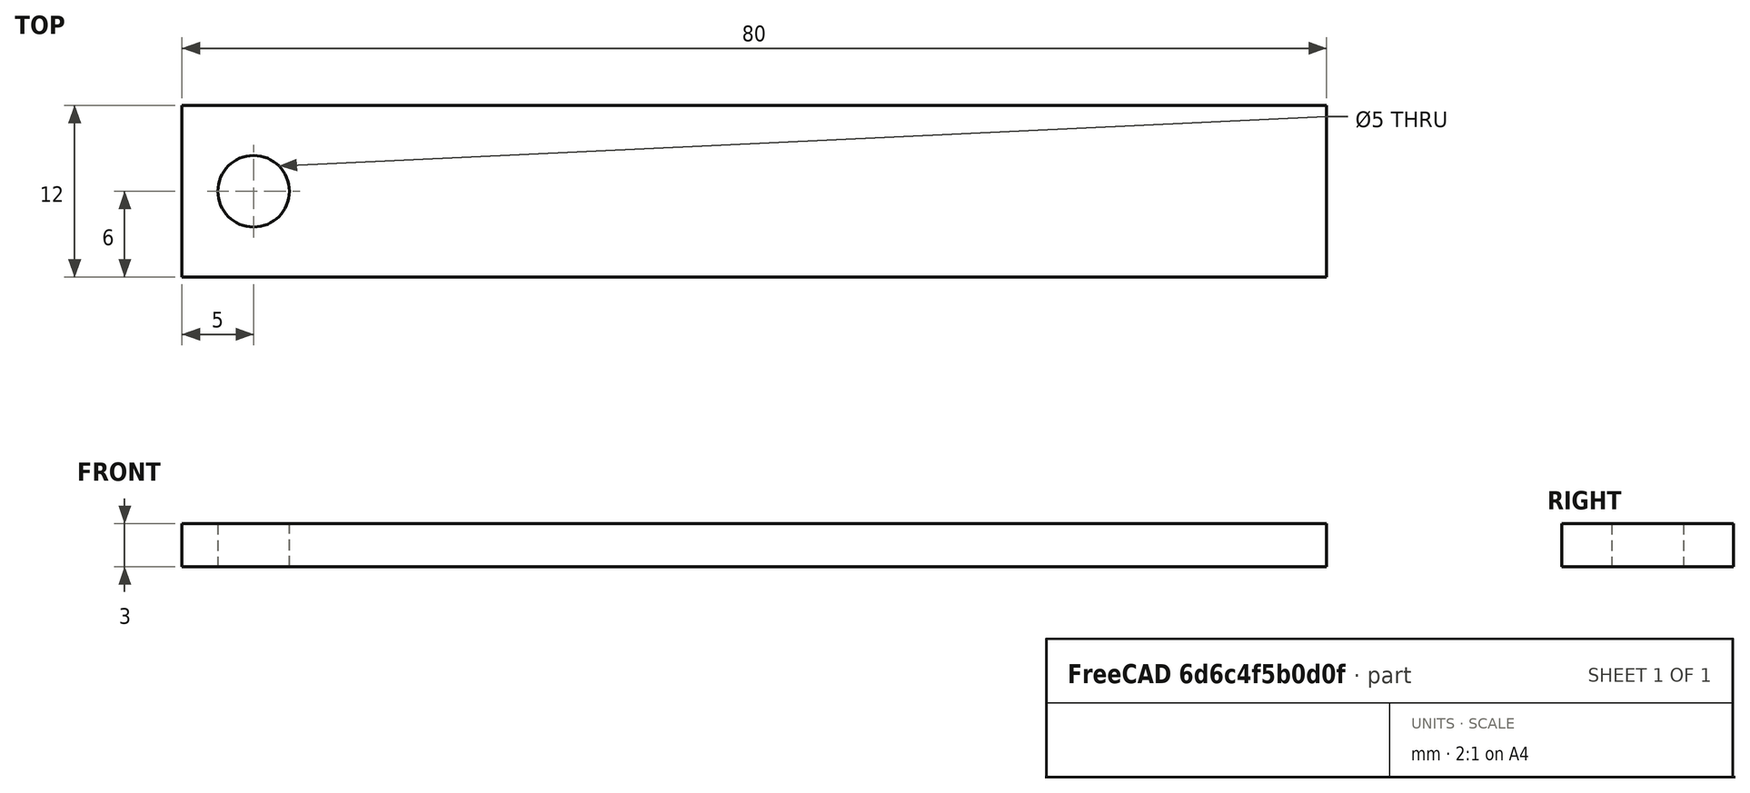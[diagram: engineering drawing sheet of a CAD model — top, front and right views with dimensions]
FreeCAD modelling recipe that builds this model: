
FCSTD DOCUMENT  (FreeCAD 0.20R29177 +426 (Git))
Label: rectangle
License: All rights reserved
LicenseURL: http://en.wikipedia.org/wiki/All_rights_reserved
objects: Sketcher::SketchObject×1, Part::Extrusion×1, PartDesign::Line×1, App::Part×1
note: 3 computed .brp shape members not serialized (recipe doc carries the construction recipe); baked Part::Feature solids carry a one-line shape summary decoded from their .brp

FEATURE [Sketcher::SketchObject] Sketch
  FullyConstrained = true
  sketch-geometry (6):
    g0: LineSegment StartX=40 StartY=-6 StartZ=0 EndX=40 EndY=6 EndZ=0
    g1: LineSegment StartX=40 StartY=6 StartZ=0 EndX=-40 EndY=6 EndZ=0
    g2: LineSegment StartX=-40 StartY=6 StartZ=0 EndX=-40 EndY=-6 EndZ=0
    g3: LineSegment StartX=-40 StartY=-6 StartZ=0 EndX=40 EndY=-6 EndZ=0
    g4: GeomPoint X=0 Y=0 Z=0
    g5: Circle CenterX=-35 CenterY=0 CenterZ=0 NormalX=0 NormalY=0 NormalZ=1 AngleXU=0 Radius=2.5
  constraints (15):
    c: Coincident(g0,g1)
    c: Coincident(g1,g2)
    c: Coincident(g2,g3)
    c: Coincident(g3,g0)
    c: Horizontal(g1)
    c: Horizontal(g3)
    c: Vertical(g0)
    c: Vertical(g2)
    c: Symmetric(g1,g0,g4)
    c: Coincident(g4,g-1)
    c: DistanceX(g1,g1) = 80
    c: DistanceY(g2,g2) = 12
    c: DistanceX(g1,g5) = 5
    c: PointOnObject(g5,g-1)
    c: Diameter(g5) = 5
FEATURE [Part::Extrusion] Extrude
  Base = -> Sketch
  Dir = (0,0,1)
  DirMode = 2
  FaceMakerClass = Part::FaceMakerBullseye
  LengthFwd = 3
  LengthRev = 0
  Solid = true
  Symmetric = false
FEATURE [PartDesign::Line] CircleAxis_1
  AttacherType = Attacher::AttachEngineLine
  Length = 14.0907
  MapMode = 19
  Placement = pos=(-35,0,3) rot=(0,0,1;0rad)
  ResizeMode = 1
  Support = -> [Extrude]
FEATURE [App::Part] Part  label="RectanglePart"
  Group = -> [Sketch,Extrude,CircleAxis_1]
  Origin = -> Origin
